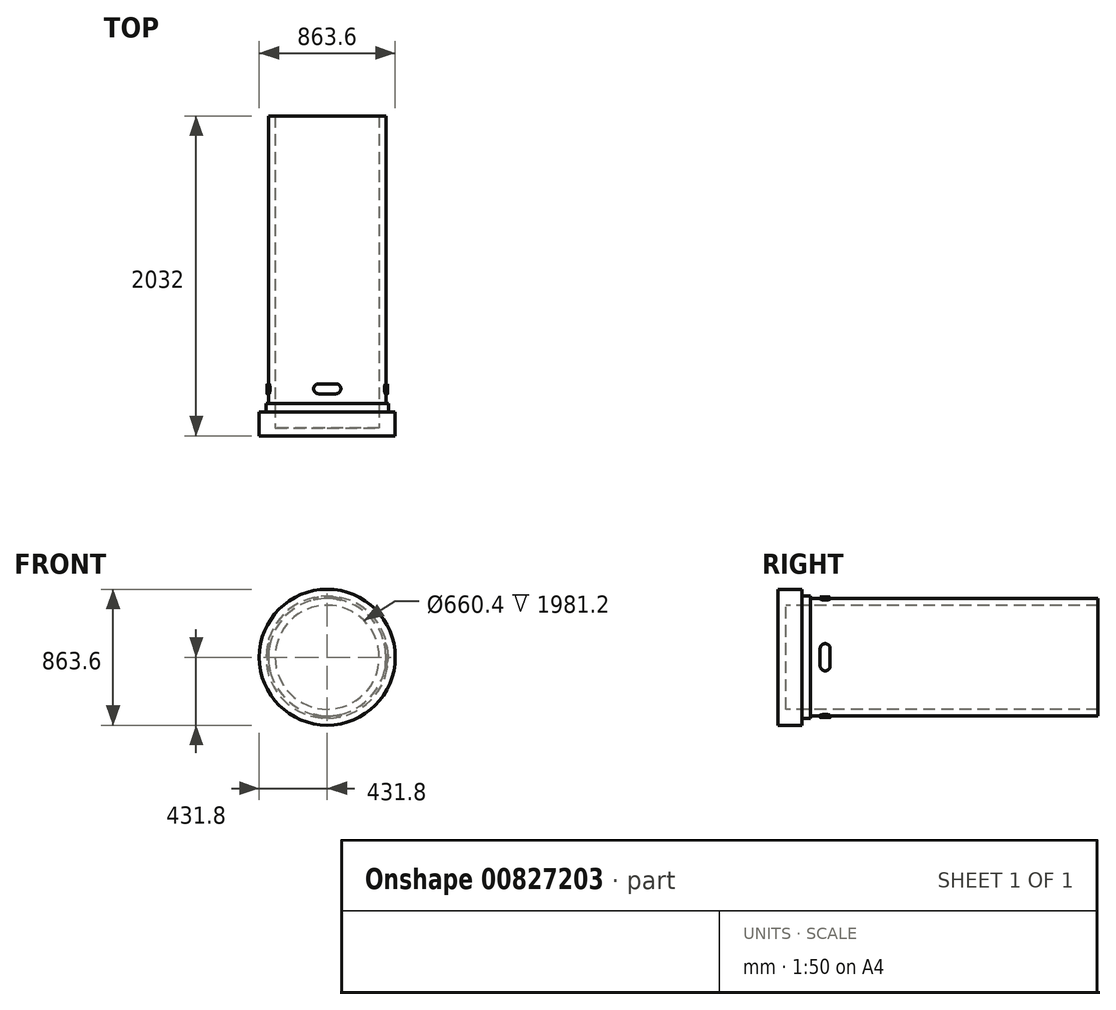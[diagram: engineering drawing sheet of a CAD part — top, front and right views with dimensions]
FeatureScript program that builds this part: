
annotation { "Feature Type Name" : "Feature", "Feature Type Description" : "" }
export const myFeature = defineFeature(function(context is Context, id is Id, definition is map)
    precondition{}
    {
        {
            var Q0;
            Q0=qCreatedBy(makeId("Front.planeOp"),FACE);
            var sketch = newSketch(context, id + "F0", { "sketchPlane" : qUnion([Q0])});
            skCircle(sketch, "E0", {"center": v(0, 0) * mm, "radius": 373.38 * mm});
            skCircle(sketch, "E1", {"center": v(0, 0) * mm, "radius": 388.62 * mm});
            skCircle(sketch, "E2", {"center": v(0, 0) * mm, "radius": 383.54 * mm});
            skCircle(sketch, "E3", {"center": v(0, 0) * mm, "radius": 431.8 * mm});
            skCircle(sketch, "E4", {"center": v(0, 0) * mm, "radius": 330.2 * mm});
            skSolve(sketch);
        }
        {
            var Q0;
            Q0=qCreatedBy(makeId("Right.planeOp"),FACE);
            var sketch = newSketch(context, id + "F1", { "sketchPlane" : qUnion([Q0])});
            skLineSegment(sketch, "E5", {"start": v(266.7, 0) * mm, "end": v(266.7, 54.61) * mm});
            skLineSegment(sketch, "E6.left", {"start": v(266.7, 54.61) * mm, "end": v(266.7, -54.6) * mm});
            skLineSegment(sketch, "E6.right", {"start": v(330.2, 54.61) * mm, "end": v(330.2, -54.61) * mm});
            skArc(sketch, "E7", {"start": v(330.2, 54.61) * mm, "mid": v(298.45, 86.36) * mm, "end": v(266.7, 54.61) * mm});
            skArc(sketch, "E8", {"start": v(266.7, -54.6) * mm, "mid": v(298.45, -86.36) * mm, "end": v(330.2, -54.61) * mm});
            skPoint(sketch, "E9.orphan", {"position": v(330.2, -86.36) * mm});
            skPoint(sketch, "E10.orphan", {"position": v(266.7, -86.36) * mm});
            skPoint(sketch, "E11.orphan", {"position": v(330.2, 86.36) * mm});
            skPoint(sketch, "E6.bottom.end.orphan", {"position": v(298.45, 86.36) * mm});
            skPoint(sketch, "E12.orphan", {"position": v(266.7, 86.36) * mm});
            skPoint(sketch, "E13.start.orphan", {"position": v(298.45, -86.36) * mm});
            skSolve(sketch);
        }
        {
            var Q0;
            Q0=qCreatedBy(makeId("Top.planeOp"),FACE);
            var sketch = newSketch(context, id + "F2", { "sketchPlane" : qUnion([Q0])});
            skLineSegment(sketch, "E14", {"start": v(0, 266.7) * mm, "end": v(54.6, 266.7) * mm});
            skLineSegment(sketch, "E15.bottom", {"start": v(54.6, 266.7) * mm, "end": v(-54.61, 266.7) * mm});
            skLineSegment(sketch, "E15.top", {"start": v(54.6, 330.2) * mm, "end": v(-54.61, 330.2) * mm});
            skArc(sketch, "E16", {"start": v(54.6, 266.7) * mm, "mid": v(86.36, 298.45) * mm, "end": v(54.61, 330.2) * mm});
            skArc(sketch, "E17", {"start": v(-54.61, 330.2) * mm, "mid": v(-86.36, 298.45) * mm, "end": v(-54.61, 266.7) * mm});
            skPoint(sketch, "E18.orphan", {"position": v(-86.36, 266.7) * mm});
            skPoint(sketch, "E19.orphan", {"position": v(-86.36, 330.2) * mm});
            skPoint(sketch, "E20.start.orphan", {"position": v(-86.36, 298.45) * mm});
            skPoint(sketch, "E21.orphan", {"position": v(86.36, 330.2) * mm});
            skPoint(sketch, "E15.left.end.orphan", {"position": v(86.36, 298.45) * mm});
            skPoint(sketch, "E22.orphan", {"position": v(86.36, 266.7) * mm});
            skSolve(sketch);
        }
        {
            var Q0;
            Q0=makeQuery(id+"F2.imprint","IMPRINT",FACE,{"disambiguationData":[TD([[makeQuery(id+"F2.imprint","IMPRINT",EDGE,{"derivedFrom":sQuery(id+"F2.wireOp",EDGE,"E15.top")}),1.0]])]});
            extrude(context, id + "F3", {"entities" : qUnion([Q0]), "endBound" : BoundingType.SYMMETRIC, "depth" : 787.4 * mm, "offsetDistance" : 25.4 * mm});
        }
        {
            var Q0;
            Q0=makeQuery(id+"F1.imprint","IMPRINT",FACE,{"disambiguationData":[TD([[makeQuery(id+"F1.imprint","IMPRINT",EDGE,{"derivedFrom":sQuery(id+"F1.wireOp",EDGE,"E6.right")}),-1.0]])]});
            extrude(context, id + "F4", {"entities" : qUnion([Q0]), "operationType" : NewBodyOperationType.ADD, "endBound" : BoundingType.SYMMETRIC, "depth" : 787.4 * mm, "offsetDistance" : 25.4 * mm});
        }
        {
            var Q0;
            Q0=makeQuery(id+"F0.imprint","IMPRINT",FACE,{"disambiguationData":[TD([[makeQuery(id+"F0.imprint","IMPRINT",EDGE,{"derivedFrom":sQuery(id+"F0.wireOp",EDGE,"E4")}),1.0]])]});
            extrude(context, id + "F5", {"entities" : qUnion([Q0]), "operationType" : NewBodyOperationType.REMOVE, "oppositeDirection" : true, "depth" : 381 * mm, "offsetDistance" : 25.4 * mm});
        }
        {
            var Q0;
            Q0=makeQuery(id+"F0.imprint","IMPRINT",FACE,{"disambiguationData":[TD([[makeQuery(id+"F0.imprint","IMPRINT",EDGE,{"derivedFrom":sQuery(id+"F0.wireOp",EDGE,"E1")}),-1.0]])]});
            var Q1;
            Q1=makeQuery(id+"F0.imprint","IMPRINT",FACE,{"disambiguationData":[TD([[makeQuery(id+"F0.imprint","IMPRINT",EDGE,{"derivedFrom":sQuery(id+"F0.wireOp",EDGE,"E1")}),1.0]])]});
            extrude(context, id + "F6", {"entities" : qUnion([Q0, Q1]), "operationType" : NewBodyOperationType.REMOVE, "oppositeDirection" : true, "depth" : 381 * mm, "offsetDistance" : 25.4 * mm});
        }
        {
            var Q0;
            Q0=makeQuery(id+"F0.imprint","IMPRINT",FACE,{"disambiguationData":[TD([[makeQuery(id+"F0.imprint","IMPRINT",EDGE,{"derivedFrom":sQuery(id+"F0.wireOp",EDGE,"E0")}),1.0]])]});
            extrude(context, id + "F7", {"entities" : qUnion([Q0]), "operationType" : NewBodyOperationType.ADD, "oppositeDirection" : true, "depth" : 2032 * mm, "offsetDistance" : 25.4 * mm});
        }
        {
            var Q0;
            Q0=makeQuery(id+"F0.imprint","IMPRINT",FACE,{"disambiguationData":[TD([[makeQuery(id+"F0.imprint","IMPRINT",EDGE,{"derivedFrom":sQuery(id+"F0.wireOp",EDGE,"E1")}),1.0]])]});
            var Q1;
            Q1=makeQuery(id+"F0.imprint","IMPRINT",FACE,{"disambiguationData":[TD([[makeQuery(id+"F0.imprint","IMPRINT",EDGE,{"derivedFrom":sQuery(id+"F0.wireOp",EDGE,"E0")}),-1.0]])]});
            extrude(context, id + "F8", {"entities" : qUnion([Q0, Q1]), "operationType" : NewBodyOperationType.ADD, "oppositeDirection" : true, "depth" : 205.74 * mm, "offsetDistance" : 25.4 * mm});
        }
        {
            var Q0;
            Q0=makeQuery(id+"F0.imprint","IMPRINT",FACE,{"disambiguationData":[TD([[makeQuery(id+"F0.imprint","IMPRINT",EDGE,{"derivedFrom":sQuery(id+"F0.wireOp",EDGE,"E1")}),-1.0]])]});
            extrude(context, id + "F9", {"entities" : qUnion([Q0]), "operationType" : NewBodyOperationType.ADD, "oppositeDirection" : true, "depth" : 152.4 * mm, "offsetDistance" : 25.4 * mm});
        }
        {
            var Q0;
            Q0=makeQuery(id+"F0.imprint","IMPRINT",FACE,{"disambiguationData":[TD([[makeQuery(id+"F0.imprint","IMPRINT",EDGE,{"derivedFrom":sQuery(id+"F0.wireOp",EDGE,"E4")}),1.0]])]});
            extrude(context, id + "F10", {"entities" : qUnion([Q0]), "operationType" : NewBodyOperationType.ADD, "oppositeDirection" : true, "depth" : 50.8 * mm, "offsetDistance" : 25.4 * mm});
        }
    });
